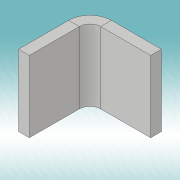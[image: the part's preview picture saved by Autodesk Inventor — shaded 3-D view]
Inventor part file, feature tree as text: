
AUTODESK INVENTOR PART (.ipt)
format: ipt  version: 2019 (Build 230136000, 136)  size: 133,632 bytes
history: native  units: mm
features: sketch x4, extrude x3, sheet_metal_op x3, other x1
ambient origin geometry x8: Origin, YZ Plane, XZ Plane, XY Plane, X Axis, Y Axis, Z Axis, Center Point
bodies: Solid1 (feature_tree)
feature tree (11):
  extrude  "Extrusion1"  Depth=10.0mm
  sheet_metal_op  "Flange1"
  extrude  "Extrusion2"  Depth=1.5mm
  extrude  "Extrusion3"  Depth=1.5mm
  sketch  "Sketch1"  dims[d0=10.0mm d1=10.0mm]
  sketch  "Sketch2"  dims[d2=1.5mm d3=0.0mm d4=1.5mm]
  other  "Plate1"
  sheet_metal_op  "Bend1"
  sheet_metal_op  "Corner1"
  sketch  "Sketch3"  dims[d5=1.5mm d6=0.75mm]
  sketch  "Sketch4"  dims[d7=3.0mm d8=1.5mm d9=10.0mm d10=90.0deg d11=1.5mm d12=6.0mm d13=1.5mm d14=1.5mm d15=2.0mm d16=3.5mm d17=5.0mm d18=0.1mm d19=0.0mm d20=2.0mm d21=5.0mm d22=3.5mm d23=0.1mm d24=0.0mm]
